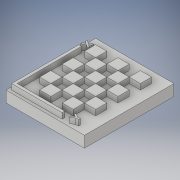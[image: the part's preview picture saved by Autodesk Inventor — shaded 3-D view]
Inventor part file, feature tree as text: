
AUTODESK INVENTOR PART (.ipt)
format: ipt  version: 2019 (Build 230136000, 136)  size: 262,144 bytes
history: native  units: in
note: dims shown in document units (in); Inventor stores cm internally (conversion verified against a paired STEP export)
features: extrude x4, sketch x4
ambient origin geometry x8: Origin, YZ Plane, XZ Plane, XY Plane, X Axis, Y Axis, Z Axis, Center Point
bodies: Solid1 (feature_tree)
feature tree (8):
  extrude  "Extrusion1"  Depth=6.2992in
  extrude  "Extrusion2"  Depth=3.1496in
  sketch  "Sketch3"  dims[d6=0.7874in d7=0.0in d8=3.937in]
  extrude  "Extrusion5"  Depth=3.937in
  extrude  "Extrusion4"  Depth=0.3937in TaperAngle=0.0deg
  sketch  "Sketch1"  dims[d0=5.5118in d1=6.2992in]
  sketch  "Sketch2"  dims[d4=2.7559in d5=3.1496in]
  sketch  "Sketch4"  dims[d9=4.7244in d10=0.3937in d11=0.0in d12=0.7874in d13=0.7874in d14=0.7874in d15=0.7874in d16=0.7874in d17=0.7874in d18=0.7874in d19=0.7874in d20=0.7874in d21=0.7874in d22=0.7874in d23=0.7874in d25=0.7874in d26=0.7874in d27=0.7874in d28=0.7874in d29=0.7874in d30=0.7874in d31=0.7874in d32=0.7874in d33=0.7874in d34=0.7874in d35=0.7874in d36=0.7874in d37=0.7874in d38=0.7874in d39=0.7874in d40=0.7874in d41=0.7874in d42=0.7874in d43=0.7874in d44=0.7874in d45=0.7874in d46=0.7874in d47=0.7874in d48=0.7874in d49=0.7874in d50=0.7874in d53=0.1969in d54=0.1969in d55=0.1969in d56=0.1969in d57=4.7244in d58=3.5433in d59=0.3937in d60=0.3937in d62=0.3996in d63=0.4823in d64=0.1998in d65=0.2412in d68=0.2239in d70=0.2446in d71=0.2239in d73=0.1969in d74=0.1969in d75=0.3937in d76=0.0in d77=0.7874in d78=0.7874in d79=0.7874in d80=0.7874in d81=0.7874in d82=0.7874in d83=0.7874in d84=0.7874in d85=0.7874in d86=0.3937in d87=0.0in]
